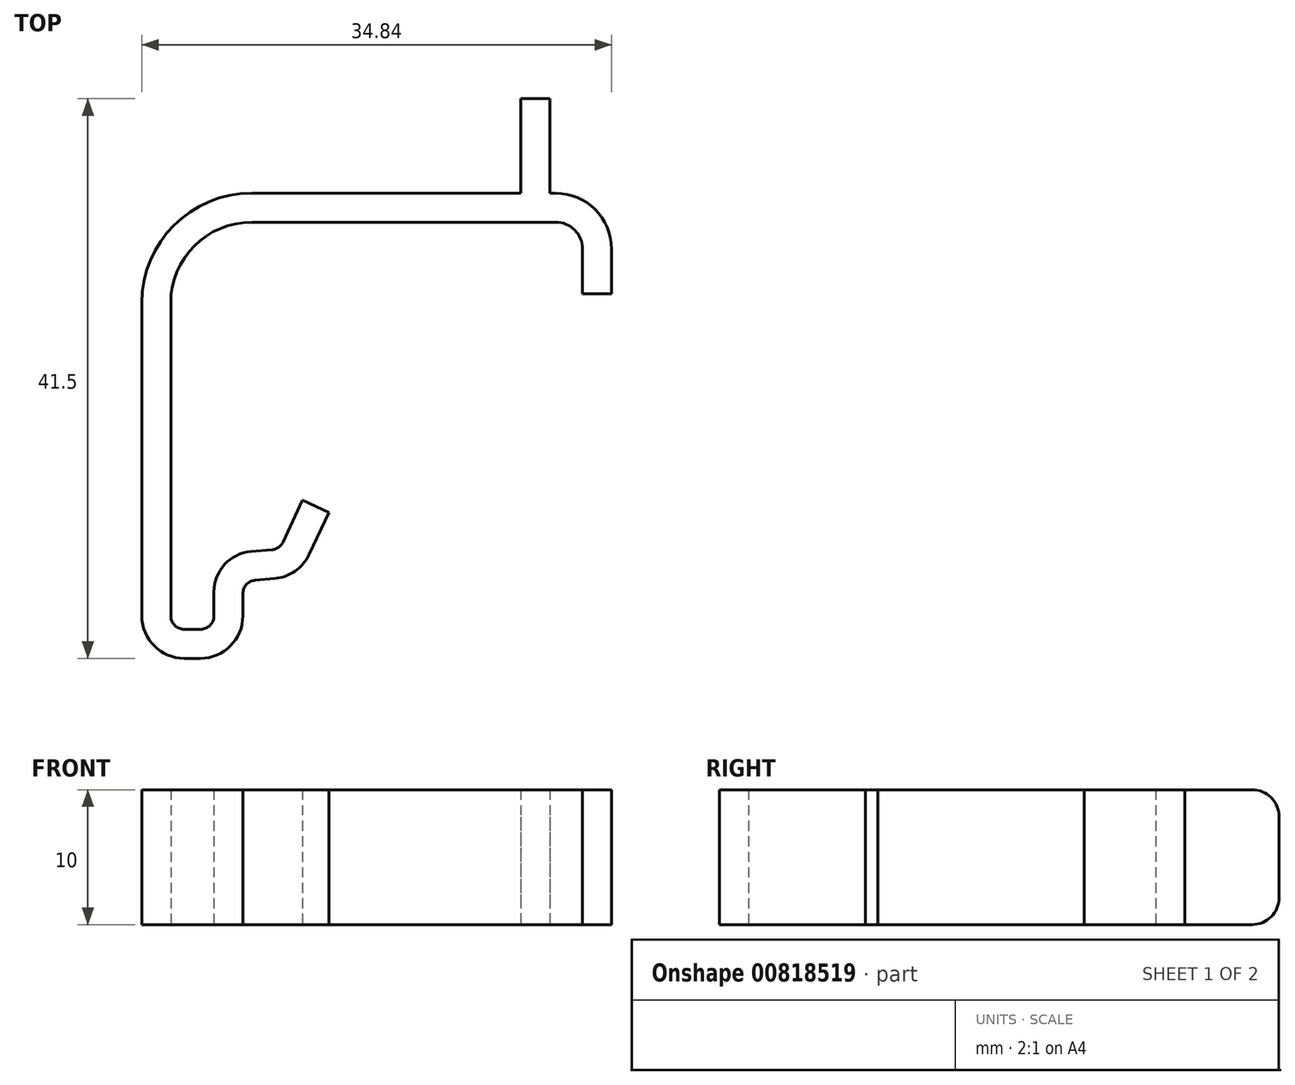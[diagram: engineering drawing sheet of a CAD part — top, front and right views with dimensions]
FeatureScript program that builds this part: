
annotation { "Feature Type Name" : "Feature", "Feature Type Description" : "" }
export const myFeature = defineFeature(function(context is Context, id is Id, definition is map)
    precondition{}
    {
        {
            var Q0;
            Q0=qCreatedBy(makeId("Top.planeOp"),FACE);
            var sketch = newSketch(context, id + "F0", { "sketchPlane" : qUnion([Q0])});
            skLineSegment(sketch, "E0", {"start": v(0, 1) * mm, "end": v(0, 24.2) * mm});
            skLineSegment(sketch, "E1", {"start": v(6, 30.2) * mm, "end": v(28.54, 30.2) * mm});
            skLineSegment(sketch, "E2", {"start": v(30.54, 28.2) * mm, "end": v(30.54, 24.9) * mm});
            skLineSegment(sketch, "E3", {"start": v(1, 0) * mm, "end": v(2.2, 0) * mm});
            skLineSegment(sketch, "E4", {"start": v(3.2, 1) * mm, "end": v(3.2, 2.78) * mm});
            skLineSegment(sketch, "E5", {"start": v(5.94, 5.77) * mm, "end": v(7.5, 5.9) * mm});
            skLineSegment(sketch, "E6", {"start": v(8.33, 6.48) * mm, "end": v(9.77, 9.58) * mm});
            skLineSegment(sketch, "E7", {"start": v(9.77, 9.58) * mm, "end": v(11.72, 8.67) * mm});
            skLineSegment(sketch, "E8", {"start": v(32.3, 5.53) * mm, "end": v(-18.06, 5.53) * mm, "construction": true});
            skLineSegment(sketch, "E9.0", {"start": v(32.7, 28.2) * mm, "end": v(32.7, 24.9) * mm});
            skLineSegment(sketch, "E9.1", {"start": v(6, 32.35) * mm, "end": v(28.54, 32.35) * mm});
            skLineSegment(sketch, "E9.2", {"start": v(-2.15, 1) * mm, "end": v(-2.15, 24.2) * mm});
            skLineSegment(sketch, "E9.3", {"start": v(1, -2.15) * mm, "end": v(2.2, -2.15) * mm});
            skLineSegment(sketch, "E9.5", {"start": v(10.27, 5.57) * mm, "end": v(11.72, 8.67) * mm});
            skLineSegment(sketch, "E9.6", {"start": v(6.26, 3.64) * mm, "end": v(7.7, 3.77) * mm});
            skLineSegment(sketch, "E9.7", {"start": v(5.35, 1) * mm, "end": v(5.35, 2.64) * mm});
            skLineSegment(sketch, "E10", {"start": v(30.54, 24.9) * mm, "end": v(32.7, 24.9) * mm});
            skPoint(sketch, "E11.visualSharp", {"position": v(0, 30.2) * mm});
            skArc(sketch, "E11.filletArc", {"start": v(6, 30.2) * mm, "mid": v(1.76, 28.44) * mm, "end": v(0, 24.2) * mm});
            skPoint(sketch, "E12.visualSharp", {"position": v(-2.15, 32.35) * mm});
            skArc(sketch, "E12.filletArc", {"start": v(6, 32.35) * mm, "mid": v(0.24, 29.96) * mm, "end": v(-2.15, 24.2) * mm});
            skPoint(sketch, "E13.visualSharp", {"position": v(30.54, 30.2) * mm});
            skArc(sketch, "E13.filletArc", {"start": v(30.54, 28.2) * mm, "mid": v(29.95, 29.61) * mm, "end": v(28.54, 30.2) * mm});
            skPoint(sketch, "E14.visualSharp", {"position": v(32.7, 32.35) * mm});
            skArc(sketch, "E14.filletArc", {"start": v(32.7, 28.2) * mm, "mid": v(31.47, 31.13) * mm, "end": v(28.54, 32.35) * mm});
            skPoint(sketch, "E15.visualSharp", {"position": v(0, 0) * mm});
            skArc(sketch, "E15.filletArc", {"start": v(0, 1) * mm, "mid": v(0.3, 0.3) * mm, "end": v(1, 0) * mm});
            skPoint(sketch, "E16.visualSharp", {"position": v(3.2, 0) * mm});
            skArc(sketch, "E16.filletArc", {"start": v(2.2, 0) * mm, "mid": v(2.9, 0.3) * mm, "end": v(3.2, 1) * mm});
            skPoint(sketch, "E17.visualSharp", {"position": v(-2.15, -2.15) * mm});
            skArc(sketch, "E17.filletArc", {"start": v(-2.15, 1) * mm, "mid": v(-1.23, -1.23) * mm, "end": v(1, -2.15) * mm});
            skPoint(sketch, "E18.visualSharp", {"position": v(5.35, -2.15) * mm});
            skArc(sketch, "E18.filletArc", {"start": v(2.2, -2.15) * mm, "mid": v(4.43, -1.23) * mm, "end": v(5.35, 1) * mm});
            skPoint(sketch, "E19.visualSharp", {"position": v(3.2, 5.53) * mm});
            skArc(sketch, "E19.filletArc", {"start": v(5.94, 5.77) * mm, "mid": v(3.99, 4.8) * mm, "end": v(3.2, 2.78) * mm});
            skPoint(sketch, "E20.visualSharp", {"position": v(5.35, 3.56) * mm});
            skArc(sketch, "E20.filletArc", {"start": v(6.26, 3.64) * mm, "mid": v(5.61, 3.32) * mm, "end": v(5.35, 2.64) * mm});
            skPoint(sketch, "E21.visualSharp", {"position": v(8.08, 5.96) * mm});
            skArc(sketch, "E21.filletArc", {"start": v(7.5, 5.9) * mm, "mid": v(8, 6.08) * mm, "end": v(8.33, 6.48) * mm});
            skPoint(sketch, "E22.visualSharp", {"position": v(9.5, 3.92) * mm});
            skArc(sketch, "E22.filletArc", {"start": v(7.7, 3.77) * mm, "mid": v(9.23, 4.32) * mm, "end": v(10.27, 5.57) * mm});
            skLineSegment(sketch, "E23.bottom", {"start": v(28.11, 32.35) * mm, "end": v(25.96, 32.35) * mm});
            skLineSegment(sketch, "E23.top", {"start": v(28.11, 39.35) * mm, "end": v(25.96, 39.35) * mm});
            skLineSegment(sketch, "E23.left", {"start": v(28.11, 32.35) * mm, "end": v(28.11, 39.35) * mm});
            skLineSegment(sketch, "E23.right", {"start": v(25.96, 32.35) * mm, "end": v(25.96, 39.35) * mm});
            skSolve(sketch);
        }
        {
            var Q0;
            Q0 = qSketchRegion(id + "F0", true);
            extrude(context, id + "F1", {"entities" : qUnion([Q0]), "depth" : 10 * mm, "offsetDistance" : 25 * mm});
        }
        {
            var Q0;
            Q0=makeQuery(id+"F1.opExtrude","CAP_EDGE",EDGE,{"disambiguationData":[OSD([sQuery(id+"F0.wireOp",EDGE,"E23.top")])],"isStart":false});
            var Q1;
            Q1=makeQuery(id+"F1.opExtrude","CAP_EDGE",EDGE,{"disambiguationData":[OSD([sQuery(id+"F0.wireOp",EDGE,"E23.top")])],"isStart":true});
            fillet(context, id + "F2", {"entities" : qUnion([Q0, Q1]), "radius" : 2 * mm, "tangentPropagation" : true, "allowEdgeOverflow" : false});
        }
    });
